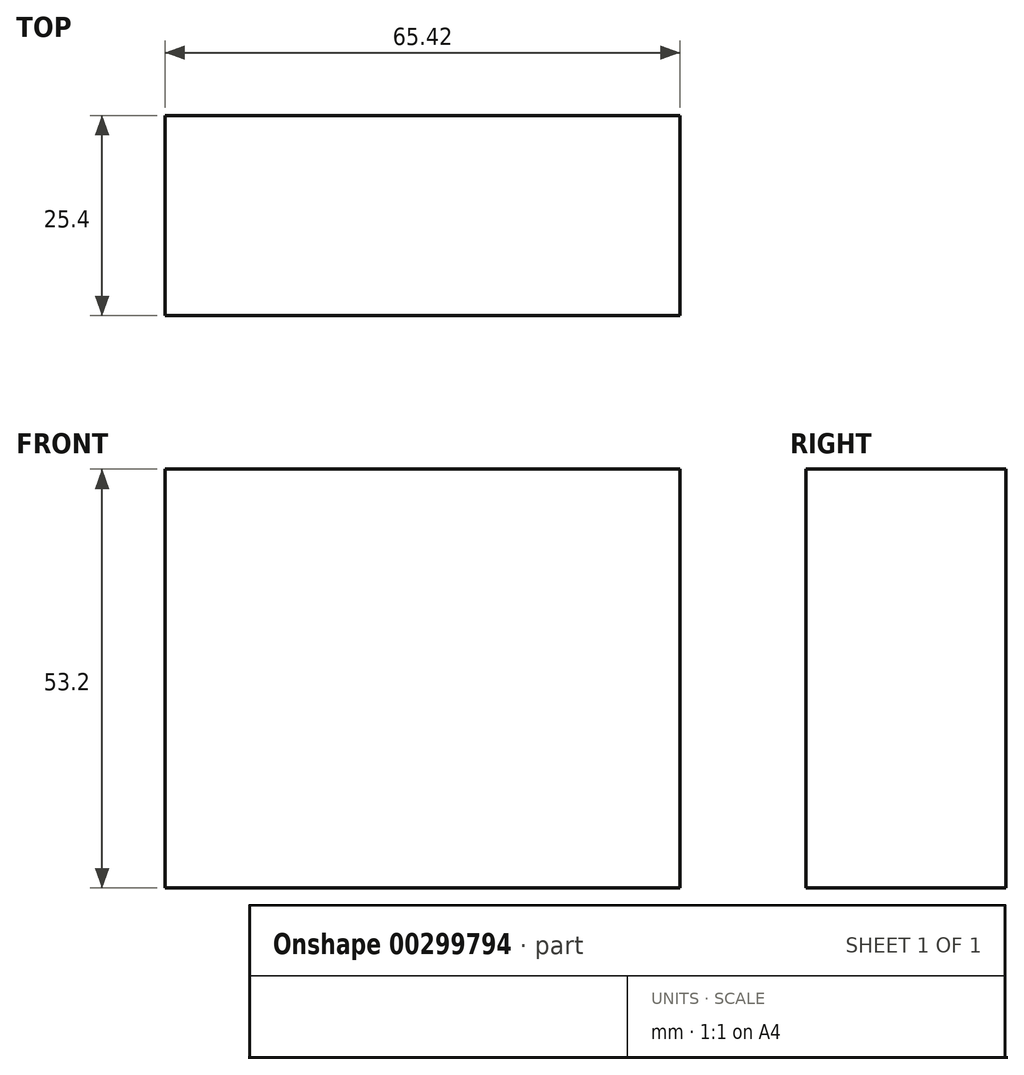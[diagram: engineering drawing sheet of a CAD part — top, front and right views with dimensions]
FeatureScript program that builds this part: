
annotation { "Feature Type Name" : "Feature", "Feature Type Description" : "" }
export const myFeature = defineFeature(function(context is Context, id is Id, definition is map)
    precondition{}
    {
        {
            var Q0;
            Q0=qCreatedBy(makeId("Front.planeOp"),FACE);
            var sketch = newSketch(context, id + "F0", { "sketchPlane" : qUnion([Q0])});
            skLineSegment(sketch, "E0.bottom", {"start": v(-32.71, 26.6) * mm, "end": v(32.71, 26.6) * mm});
            skLineSegment(sketch, "E0.top", {"start": v(-32.71, -26.6) * mm, "end": v(32.71, -26.6) * mm});
            skLineSegment(sketch, "E0.left", {"start": v(-32.71, 26.6) * mm, "end": v(-32.71, -26.6) * mm});
            skLineSegment(sketch, "E0.right", {"start": v(32.71, 26.6) * mm, "end": v(32.71, -26.6) * mm});
            skPoint(sketch, "E0.middle", {"position": v(0, 0) * mm});
            skSolve(sketch);
        }
        {
            var Q0;
            Q0=makeQuery(id+"F0.imprint","IMPRINT",FACE,{"disambiguationData":[TD([[makeQuery(id+"F0.imprint","IMPRINT",EDGE,{"derivedFrom":sQuery(id+"F0.wireOp",EDGE,"E0.bottom")}),-1.0]])]});
            extrude(context, id + "F1", {"entities" : qUnion([Q0]), "depth" : 25.4 * mm});
        }
    });
